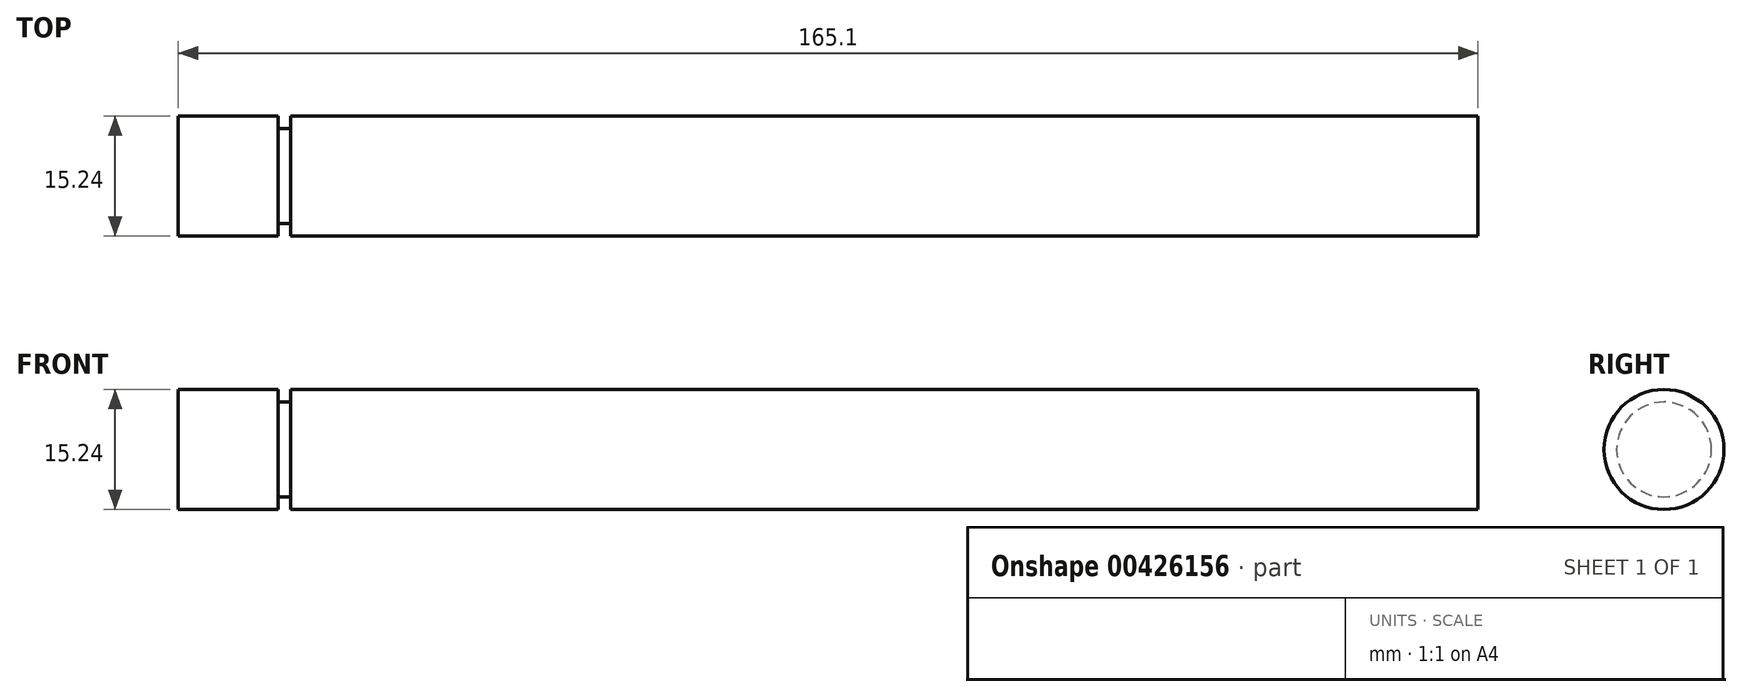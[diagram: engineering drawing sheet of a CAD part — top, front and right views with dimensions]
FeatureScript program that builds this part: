
annotation { "Feature Type Name" : "Feature", "Feature Type Description" : "" }
export const myFeature = defineFeature(function(context is Context, id is Id, definition is map)
    precondition{}
    {
        {
            var Q0;
            Q0=qCreatedBy(makeId("Right.planeOp"),FACE);
            var sketch = newSketch(context, id + "F0", { "sketchPlane" : qUnion([Q0])});
            skCircle(sketch, "E0", {"center": v(0, 0) * mm, "radius": 7.62 * mm});
            skSolve(sketch);
        }
        {
            var Q0;
            Q0 = qSketchRegion(id + "F0", true);
            extrude(context, id + "F1", {"entities" : qUnion([Q0]), "depth" : 165.1 * mm, "offsetDistance" : 25.4 * mm});
        }
        {
            var Q0;
            Q0=qCreatedBy(makeId("Front.planeOp"),FACE);
            var sketch = newSketch(context, id + "F2", { "sketchPlane" : qUnion([Q0])});
            skLineSegment(sketch, "E1", {"start": v(0, 0) * mm, "end": v(18.48, 0) * mm, "construction": true});
            skLineSegment(sketch, "E2.bottom", {"start": v(12.7, 6.02) * mm, "end": v(14.3, 6.02) * mm});
            skLineSegment(sketch, "E2.top", {"start": v(12.7, 7.62) * mm, "end": v(14.3, 7.62) * mm});
            skLineSegment(sketch, "E2.left", {"start": v(12.7, 6.02) * mm, "end": v(12.7, 7.62) * mm});
            skLineSegment(sketch, "E2.right", {"start": v(14.3, 6.02) * mm, "end": v(14.3, 7.62) * mm});
            skSolve(sketch);
        }
        {
            var Q0;
            Q0 = qSketchRegion(id + "F2", true);
            var Q1;
            Q1=sQuery(id+"F2.wireOp",EDGE,"E1");
            revolve(context, id + "F3", {"operationType" : NewBodyOperationType.REMOVE, "surfaceOperationType" : NewSurfaceOperationType.NEW, "entities" : qUnion([Q0]), "axis" : qUnion([Q1]), "revolveType" : RevolveType.FULL, "oppositeDirection" : true});
        }
    });
